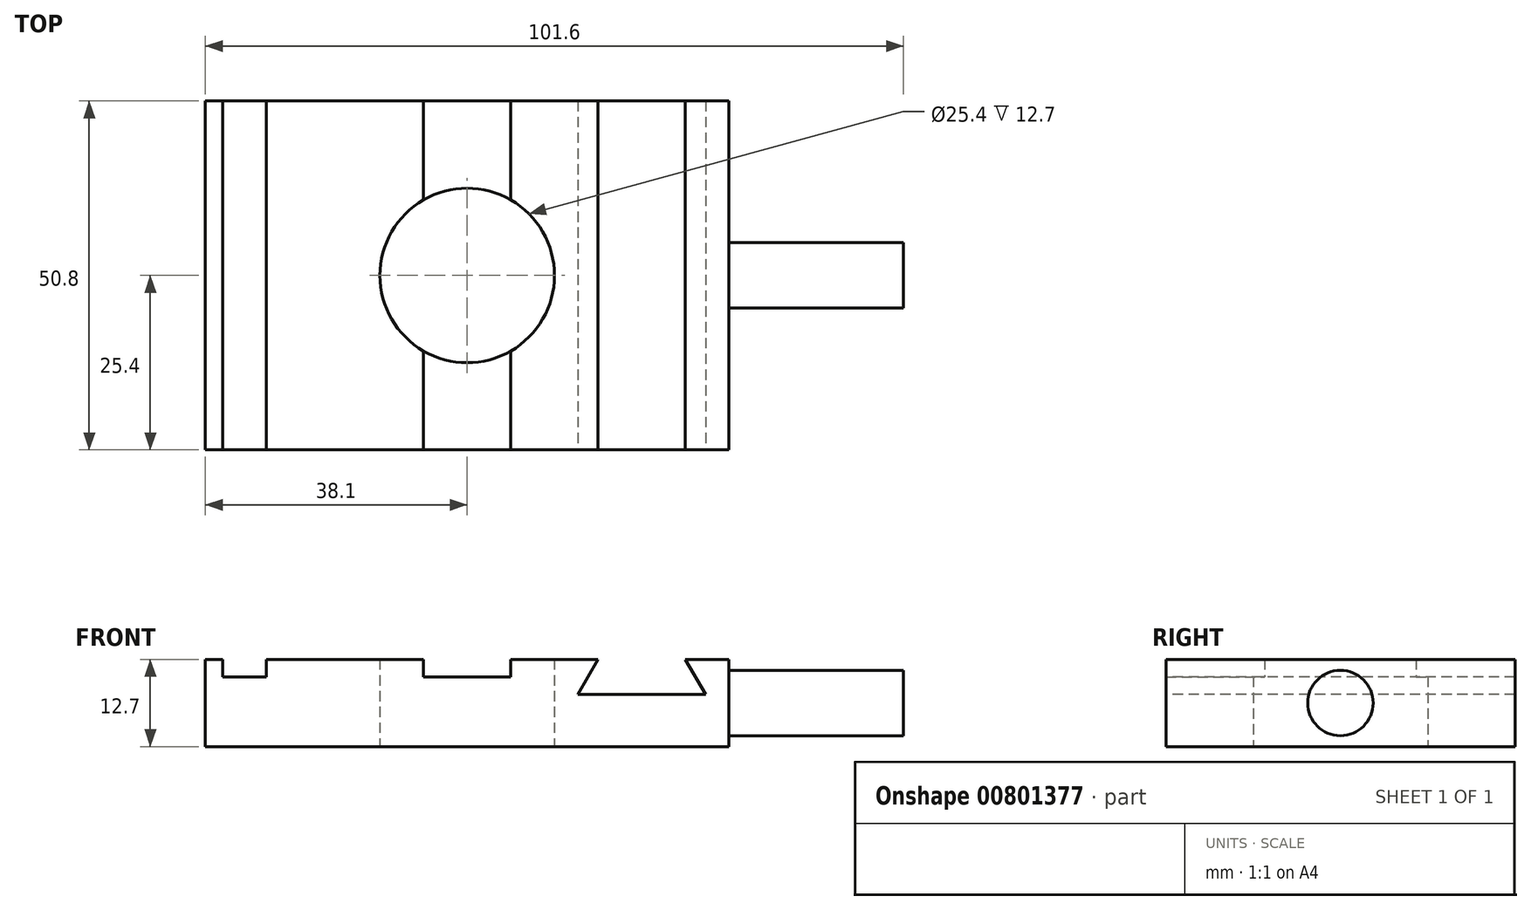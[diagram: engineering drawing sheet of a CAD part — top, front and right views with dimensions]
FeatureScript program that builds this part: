
annotation { "Feature Type Name" : "Feature", "Feature Type Description" : "" }
export const myFeature = defineFeature(function(context is Context, id is Id, definition is map)
    precondition{}
    {
        {
            var Q0;
            Q0=qCreatedBy(makeId("Top.planeOp"),FACE);
            var sketch = newSketch(context, id + "F0", { "sketchPlane" : qUnion([Q0])});
            skLineSegment(sketch, "E0.bottom", {"start": v(38.1, -25.4) * mm, "end": v(-38.1, -25.4) * mm});
            skLineSegment(sketch, "E0.top", {"start": v(38.1, 25.4) * mm, "end": v(-38.1, 25.4) * mm});
            skLineSegment(sketch, "E0.left", {"start": v(38.1, -25.4) * mm, "end": v(38.1, 25.4) * mm});
            skLineSegment(sketch, "E0.right", {"start": v(-38.1, -25.4) * mm, "end": v(-38.1, 25.4) * mm});
            skPoint(sketch, "E0.middle", {"position": v(0, 0) * mm});
            skCircle(sketch, "E1", {"center": v(0, 0) * mm, "radius": 12.7 * mm});
            skSolve(sketch);
        }
        {
            var Q0;
            Q0=makeQuery(id+"F0.imprint","IMPRINT",FACE,{"disambiguationData":[TD([[makeQuery(id+"F0.imprint","IMPRINT",EDGE,{"derivedFrom":sQuery(id+"F0.wireOp",EDGE,"E0.bottom")}),-1.0]])]});
            extrude(context, id + "F1", {"entities" : qUnion([Q0]), "depth" : 12.7 * mm, "offsetDistance" : 25.4 * mm});
        }
        {
            var Q0;
            Q0=makeQuery(id+"F1.opExtrude","CAP_FACE",FACE,{"disambiguationData":[OSD([sQuery(id+"F0.wireOp",EDGE,"E0.bottom"),sQuery(id+"F0.wireOp",EDGE,"E0.top"),sQuery(id+"F0.wireOp",EDGE,"E0.left"),sQuery(id+"F0.wireOp",EDGE,"E0.right"),sQuery(id+"F0.wireOp",EDGE,"E1")])],"isStart":false});
            var sketch = newSketch(context, id + "F2", { "sketchPlane" : qUnion([Q0])});
            skLineSegment(sketch, "E2.bottom", {"start": v(-35.56, 25.4) * mm, "end": v(-29.2, 25.4) * mm});
            skLineSegment(sketch, "E2.top", {"start": v(-35.56, -25.4) * mm, "end": v(-29.2, -25.4) * mm});
            skLineSegment(sketch, "E2.left", {"start": v(-35.56, 25.4) * mm, "end": v(-35.56, -25.4) * mm});
            skLineSegment(sketch, "E2.right", {"start": v(-29.2, 25.4) * mm, "end": v(-29.2, -25.4) * mm});
            skPoint(sketch, "E3.endSnap0", {"position": v(0, -25.4) * mm});
            skLineSegment(sketch, "E4", {"start": v(6.35, 25.4) * mm, "end": v(6.35, -25.4) * mm});
            skLineSegment(sketch, "E5", {"start": v(-6.35, -25.4) * mm, "end": v(-6.35, 25.4) * mm});
            skLineSegment(sketch, "E6", {"start": v(-6.35, 25.4) * mm, "end": v(6.35, 25.4) * mm});
            skLineSegment(sketch, "E7", {"start": v(-6.35, -25.4) * mm, "end": v(6.35, -25.4) * mm});
            skLineSegment(sketch, "E8", {"start": v(0, 25.4) * mm, "end": v(0, -25.4) * mm, "construction": true});
            skSolve(sketch);
        }
        {
            var Q0;
            Q0=makeQuery(id+"F2.imprint","IMPRINT",FACE,{"disambiguationData":[TD([[makeQuery(id+"F2.imprint","IMPRINT",EDGE,{"derivedFrom":sQuery(id+"F2.wireOp",EDGE,"E2.bottom")}),1.0]])]});
            var Q1;
            {var subQ0=sQuery(id+"F2.wireOp",EDGE,"E6");Q1=makeQuery(id+"F2.imprint","IMPRINT",FACE,{"disambiguationData":[TD([[makeQuery(id+"F2.imprint","IMPRINT",EDGE,{"derivedFrom":subQ0}),1.0]])]});}
            var Q2;
            {var subQ0=sQuery(id+"F2.wireOp",EDGE,"E4");var subQ1=makeQuery(id+"F1.opExtrude","CAP_EDGE",EDGE,{"disambiguationData":[OSD([sQuery(id+"F0.wireOp",EDGE,"E1")])],"isStart":false});var subQ2=makeQuery(id+"F2.imprint","INTERSECT",VERTEX,{"disambiguationData":[OD(0.0)],"derivedFrom":[subQ1,subQ0]});Q2=makeQuery(id+"F2.imprint","IMPRINT",FACE,{"disambiguationData":[TD([[makeQuery(id+"F2.imprint","IMPRINT",EDGE,{"disambiguationData":[TD([[subQ2,-1.0]])],"derivedFrom":subQ0}),-1.0]])]});}
            var Q3;
            {var subQ0=sQuery(id+"F2.wireOp",EDGE,"E7");Q3=makeQuery(id+"F2.imprint","IMPRINT",FACE,{"disambiguationData":[TD([[makeQuery(id+"F2.imprint","IMPRINT",EDGE,{"derivedFrom":subQ0}),-1.0]])]});}
            extrude(context, id + "F3", {"entities" : qUnion([Q0, Q1, Q2, Q3]), "operationType" : NewBodyOperationType.REMOVE, "oppositeDirection" : true, "depth" : 2.54 * mm, "offsetDistance" : 25.4 * mm});
        }
        {
            var Q0;
            Q0=makeQuery(id+"F1.opExtrude","SWEPT_FACE",FACE,{"disambiguationData":[OSD([sQuery(id+"F0.wireOp",EDGE,"E0.bottom")])]});
            var sketch = newSketch(context, id + "F4", { "sketchPlane" : qUnion([Q0])});
            skLineSegment(sketch, "E9", {"start": v(19.05, 12.7) * mm, "end": v(16.12, 7.62) * mm});
            skLineSegment(sketch, "E10", {"start": v(34.68, 7.62) * mm, "end": v(31.75, 12.7) * mm});
            skLineSegment(sketch, "E11", {"start": v(19.05, 12.7) * mm, "end": v(31.75, 12.7) * mm});
            skLineSegment(sketch, "E12", {"start": v(16.12, 7.62) * mm, "end": v(34.68, 7.62) * mm});
            skLineSegment(sketch, "E13", {"start": v(25.4, 12.7) * mm, "end": v(25.4, 7.62) * mm, "construction": true});
            skSolve(sketch);
        }
        {
            var Q0;
            Q0=makeQuery(id+"F4.imprint","IMPRINT",FACE,{"disambiguationData":[TD([[makeQuery(id+"F4.imprint","IMPRINT",EDGE,{"derivedFrom":sQuery(id+"F4.wireOp",EDGE,"E9")}),1.0]])]});
            extrude(context, id + "F5", {"entities" : qUnion([Q0]), "operationType" : NewBodyOperationType.REMOVE, "endBound" : BoundingType.THROUGH_ALL, "oppositeDirection" : true, "depth" : 25.4 * mm, "offsetDistance" : 25.4 * mm});
        }
        {
            var Q0;
            Q0=makeQuery(id+"F1.opExtrude","SWEPT_FACE",FACE,{"disambiguationData":[OSD([sQuery(id+"F0.wireOp",EDGE,"E0.left")])]});
            var sketch = newSketch(context, id + "F6", { "sketchPlane" : qUnion([Q0])});
            skCircle(sketch, "E14", {"center": v(0, 6.35) * mm, "radius": 4.76 * mm});
            skPoint(sketch, "E14.centerSnap0", {"position": v(-25.4, 6.35) * mm});
            skPoint(sketch, "E14.centerSnap1", {"position": v(0, 12.7) * mm});
            skSolve(sketch);
        }
        {
            var Q0;
            Q0=makeQuery(id+"F6.imprint","IMPRINT",FACE,{"disambiguationData":[TD([[makeQuery(id+"F6.imprint","IMPRINT",EDGE,{"derivedFrom":sQuery(id+"F6.wireOp",EDGE,"E14")}),1.0]])]});
            extrude(context, id + "F7", {"entities" : qUnion([Q0]), "operationType" : NewBodyOperationType.ADD, "depth" : 25.4 * mm, "offsetDistance" : 25.4 * mm});
        }
    });
